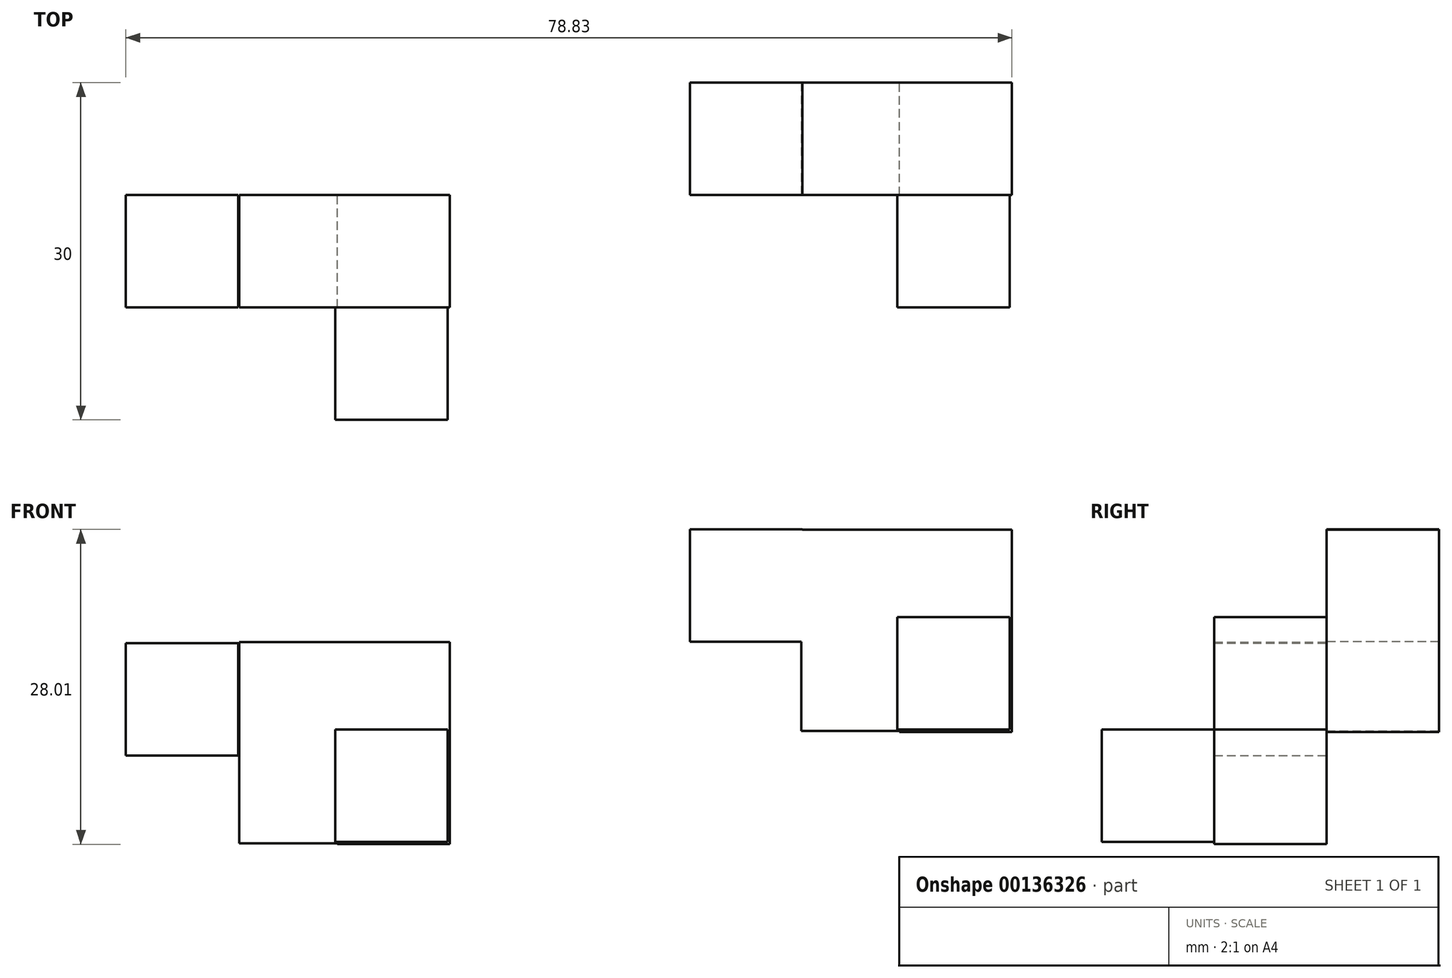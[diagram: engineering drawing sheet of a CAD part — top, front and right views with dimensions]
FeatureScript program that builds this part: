
annotation { "Feature Type Name" : "Feature", "Feature Type Description" : "" }
export const myFeature = defineFeature(function(context is Context, id is Id, definition is map)
    precondition{}
    {
        {
            var Q0;
            Q0=qCreatedBy(makeId("Front.planeOp"),FACE);
            var sketch = newSketch(context, id + "F0", { "sketchPlane" : qUnion([Q0])});
            skLineSegment(sketch, "E0.bottom", {"start": v(-25.76, -17.42) * mm, "end": v(-17.02, -17.42) * mm});
            skLineSegment(sketch, "E0.top", {"start": v(-25.76, -26.16) * mm, "end": v(-17.02, -26.16) * mm});
            skLineSegment(sketch, "E0.left", {"start": v(-25.76, -17.42) * mm, "end": v(-25.76, -26.16) * mm});
            skLineSegment(sketch, "E0.right", {"start": v(-17.02, -17.42) * mm, "end": v(-17.02, -26.16) * mm});
            skLineSegment(sketch, "E1.top", {"start": v(-25.76, -8.25) * mm, "end": v(-17.02, -8.25) * mm});
            skLineSegment(sketch, "E1.left", {"start": v(-25.76, -17.42) * mm, "end": v(-25.76, -8.25) * mm});
            skLineSegment(sketch, "E1.right", {"start": v(-17.02, -17.42) * mm, "end": v(-17.02, -8.25) * mm});
            skLineSegment(sketch, "E2.bottom", {"start": v(-17.02, -8.25) * mm, "end": v(-7.02, -8.25) * mm});
            skLineSegment(sketch, "E2.top", {"start": v(-17.02, -26.23) * mm, "end": v(-7.02, -26.23) * mm});
            skLineSegment(sketch, "E2.left", {"start": v(-17.02, -8.25) * mm, "end": v(-17.02, -26.23) * mm});
            skLineSegment(sketch, "E2.right", {"start": v(-7.02, -8.25) * mm, "end": v(-7.02, -26.23) * mm});
            skSolve(sketch);
        }
        {
            var Q0;
            Q0 = qSketchRegion(id + "F0", true);
            extrude(context, id + "F1", {"entities" : qUnion([Q0]), "depth" : 10 * mm});
        }
        {
            var Q0;
            Q0=qCreatedBy(makeId("Front.planeOp"),FACE);
            var sketch = newSketch(context, id + "F2", { "sketchPlane" : qUnion([Q0])});
            skLineSegment(sketch, "E3.bottom", {"start": v(-25.85, -8.34) * mm, "end": v(-35.85, -8.34) * mm});
            skLineSegment(sketch, "E3.top", {"start": v(-25.85, -18.34) * mm, "end": v(-35.85, -18.34) * mm});
            skLineSegment(sketch, "E3.left", {"start": v(-25.85, -8.34) * mm, "end": v(-25.85, -18.34) * mm});
            skLineSegment(sketch, "E3.right", {"start": v(-35.85, -8.34) * mm, "end": v(-35.85, -18.34) * mm});
            skSolve(sketch);
        }
        {
            var Q0;
            Q0 = qSketchRegion(id + "F2", true);
            extrude(context, id + "F3", {"entities" : qUnion([Q0]), "depth" : 10 * mm});
        }
        {
            var Q0;
            Q0=qCreatedBy(makeId("Front.planeOp"),FACE);
            var sketch = newSketch(context, id + "F4", { "sketchPlane" : qUnion([Q0])});
            skLineSegment(sketch, "E4.bottom", {"start": v(-7.23, -26.01) * mm, "end": v(-17.23, -26.01) * mm});
            skLineSegment(sketch, "E4.top", {"start": v(-7.23, -16.01) * mm, "end": v(-17.23, -16.01) * mm});
            skLineSegment(sketch, "E4.left", {"start": v(-7.23, -26.01) * mm, "end": v(-7.23, -16.01) * mm});
            skLineSegment(sketch, "E4.right", {"start": v(-17.23, -26.01) * mm, "end": v(-17.23, -16.01) * mm});
            skSolve(sketch);
        }
        {
            var Q0;
            Q0 = qSketchRegion(id + "F4", true);
            extrude(context, id + "F5", {"entities" : qUnion([Q0]), "operationType" : NewBodyOperationType.ADD, "depth" : 20 * mm});
        }
        {
            var Q0;
            Q0=makeQuery(id+"F1.opExtrude","SWEPT_BODY",BODY,{"disambiguationData":[OSD([sQuery(id+"F0.wireOp",EDGE,"E0.top"),sQuery(id+"F0.wireOp",EDGE,"E0.left"),sQuery(id+"F0.wireOp",EDGE,"E1.top"),sQuery(id+"F0.wireOp",EDGE,"E1.left"),sQuery(id+"F0.wireOp",EDGE,"E2.bottom"),sQuery(id+"F0.wireOp",EDGE,"E2.top"),sQuery(id+"F0.wireOp",EDGE,"E2.left"),sQuery(id+"F0.wireOp",EDGE,"E2.right")])]});
            transform(context, id + "F6", {"entities" : qUnion([Q0]), "transformType" : TransformType.TRANSLATION_3D, "dx" : 50 * mm, "dy" : 10 * mm, "dz" : 10 * mm, "makeCopy" : true});
        }
        {
            var Q0;
            Q0=qCreatedBy(makeId("Front.planeOp"),FACE);
            var sketch = newSketch(context, id + "F7", { "sketchPlane" : qUnion([Q0])});
            skLineSegment(sketch, "E5.bottom", {"start": v(24.33, 1.78) * mm, "end": v(14.33, 1.78) * mm});
            skLineSegment(sketch, "E5.top", {"start": v(24.33, -8.22) * mm, "end": v(14.33, -8.22) * mm});
            skLineSegment(sketch, "E5.left", {"start": v(24.33, 1.78) * mm, "end": v(24.33, -8.22) * mm});
            skLineSegment(sketch, "E5.right", {"start": v(14.33, 1.78) * mm, "end": v(14.33, -8.22) * mm});
            skSolve(sketch);
        }
        {
            var Q0;
            Q0=makeQuery(id+"F7.imprint","IMPRINT",FACE,{"disambiguationData":[TD([[makeQuery(id+"F7.imprint","IMPRINT",EDGE,{"derivedFrom":sQuery(id+"F7.wireOp",EDGE,"E5.bottom")}),1.0]])]});
            extrude(context, id + "F8", {"entities" : qUnion([Q0]), "operationType" : NewBodyOperationType.ADD, "oppositeDirection" : true, "depth" : 10 * mm});
        }
    });
